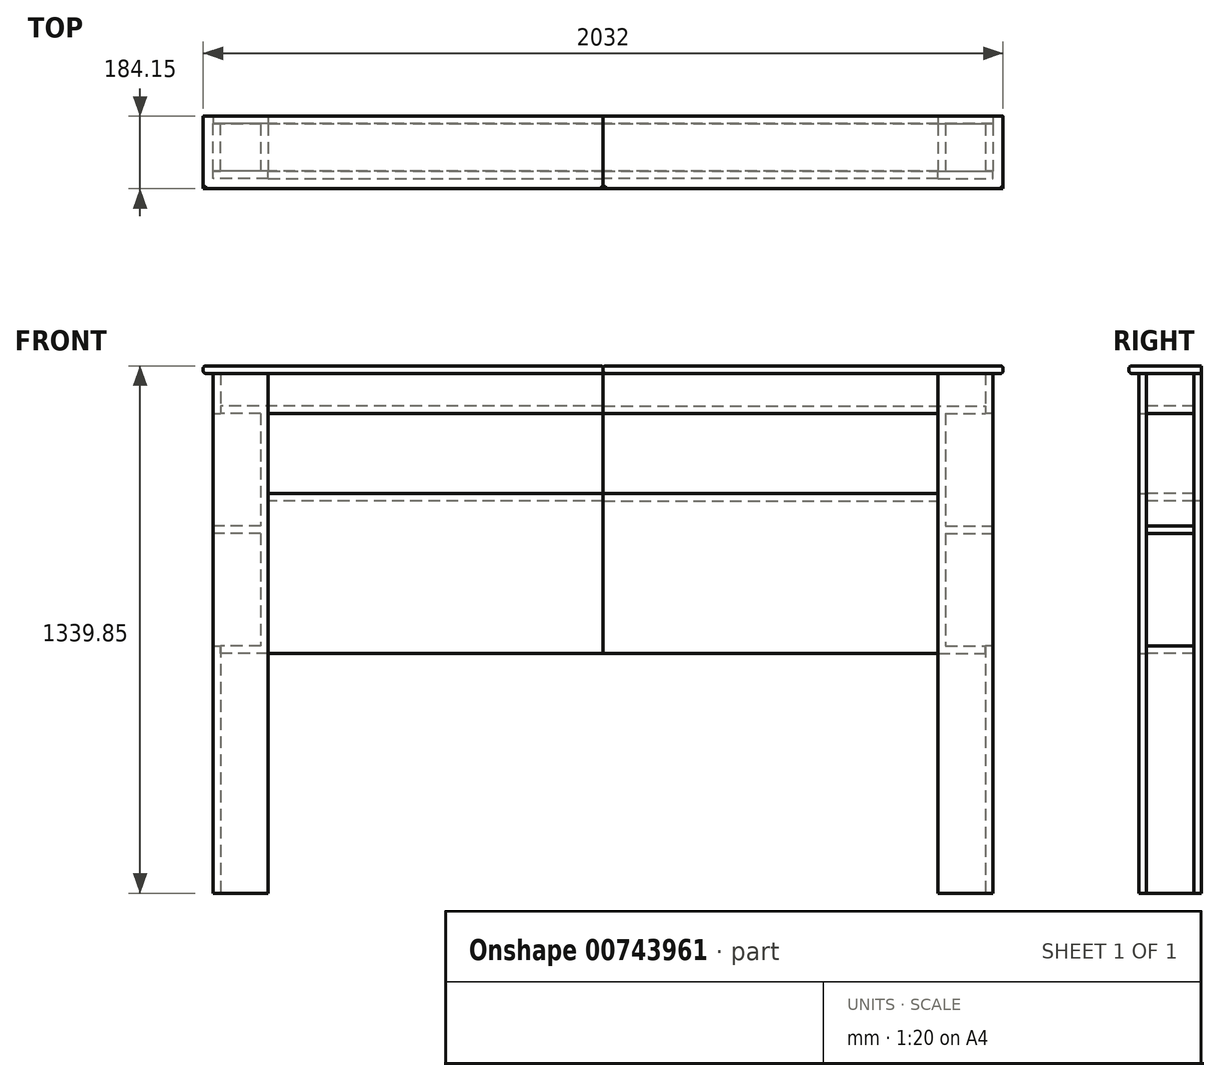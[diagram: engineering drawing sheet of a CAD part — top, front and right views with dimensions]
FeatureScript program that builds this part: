
annotation { "Feature Type Name" : "Feature", "Feature Type Description" : "" }
export const myFeature = defineFeature(function(context is Context, id is Id, definition is map)
    precondition{}
    {
        {
            var Q0;
            Q0=qCreatedBy(makeId("Front.planeOp"),FACE);
            var sketch = newSketch(context, id + "F0", { "sketchPlane" : qUnion([Q0])});
            skLineSegment(sketch, "E0.bottom", {"start": v(850.9, 0) * mm, "end": v(990.6, 0) * mm});
            skLineSegment(sketch, "E0.top", {"start": v(850.9, 1320.8) * mm, "end": v(990.6, 1320.8) * mm});
            skLineSegment(sketch, "E0.left", {"start": v(850.9, 0) * mm, "end": v(850.9, 1320.8) * mm});
            skLineSegment(sketch, "E0.right", {"start": v(990.6, 0) * mm, "end": v(990.6, 1320.8) * mm});
            skSolve(sketch);
        }
        {
            var Q0;
            Q0 = qSketchRegion(id + "F0", true);
            extrude(context, id + "F1", {"entities" : qUnion([Q0]), "depth" : 19.05 * mm, "offsetDistance" : 25.4 * mm});
        }
        {
            var Q0;
            Q0=qCreatedBy(makeId("Front.planeOp"),FACE);
            var sketch = newSketch(context, id + "F2", { "sketchPlane" : qUnion([Q0])});
            skLineSegment(sketch, "E1.bottom", {"start": v(850.9, 609.6) * mm, "end": v(0, 609.6) * mm});
            skLineSegment(sketch, "E1.top", {"start": v(850.9, 1016) * mm, "end": v(0, 1016) * mm});
            skLineSegment(sketch, "E1.left", {"start": v(850.9, 609.6) * mm, "end": v(850.9, 1016) * mm});
            skLineSegment(sketch, "E1.right", {"start": v(0, 609.6) * mm, "end": v(0, 1016) * mm});
            skSolve(sketch);
        }
        {
            var Q0;
            Q0 = qSketchRegion(id + "F2", true);
            extrude(context, id + "F3", {"entities" : qUnion([Q0]), "depth" : 19.05 * mm, "offsetDistance" : 25.4 * mm});
        }
        {
            var Q0;
            Q0=qCreatedBy(makeId("Front.planeOp"),FACE);
            var sketch = newSketch(context, id + "F4", { "sketchPlane" : qUnion([Q0])});
            skLineSegment(sketch, "E2.bottom", {"start": v(0, 1016) * mm, "end": v(850.9, 1016) * mm});
            skLineSegment(sketch, "E2.top", {"start": v(0, 996.95) * mm, "end": v(850.9, 996.95) * mm});
            skLineSegment(sketch, "E2.left", {"start": v(0, 1016) * mm, "end": v(0, 996.95) * mm});
            skLineSegment(sketch, "E3.left", {"start": v(850.9, 1219.2) * mm, "end": v(850.9, 1016) * mm});
            skLineSegment(sketch, "E3.right", {"start": v(869.95, 1219.2) * mm, "end": v(869.95, 933.57) * mm});
            skLineSegment(sketch, "E4.bottom", {"start": v(850.9, 1219.2) * mm, "end": v(0, 1219.2) * mm});
            skLineSegment(sketch, "E4.top", {"start": v(869.95, 1238.25) * mm, "end": v(0, 1238.25) * mm});
            skLineSegment(sketch, "E4.right", {"start": v(0, 1219.2) * mm, "end": v(0, 1238.25) * mm});
            skLineSegment(sketch, "E5.bottom", {"start": v(869.95, 1238.25) * mm, "end": v(971.55, 1238.25) * mm});
            skLineSegment(sketch, "E5.top", {"start": v(869.95, 1219.2) * mm, "end": v(971.55, 1219.2) * mm});
            skLineSegment(sketch, "E6", {"start": v(971.55, 1238.25) * mm, "end": v(971.55, 1219.2) * mm});
            skLineSegment(sketch, "E7", {"start": v(850.9, 609.6) * mm, "end": v(869.95, 609.6) * mm});
            skLineSegment(sketch, "E8", {"start": v(850.9, 609.6) * mm, "end": v(850.9, 996.95) * mm});
            skLineSegment(sketch, "E9.bottom", {"start": v(869.95, 609.6) * mm, "end": v(971.55, 609.6) * mm});
            skLineSegment(sketch, "E9.top", {"start": v(869.95, 628.9) * mm, "end": v(971.55, 628.9) * mm});
            skLineSegment(sketch, "E10.bottom", {"start": v(869.95, 914.52) * mm, "end": v(990.6, 914.52) * mm});
            skLineSegment(sketch, "E10.top", {"start": v(869.95, 933.57) * mm, "end": v(990.6, 933.57) * mm});
            skLineSegment(sketch, "E10.right", {"start": v(990.6, 914.52) * mm, "end": v(990.6, 933.57) * mm});
            skLineSegment(sketch, "E11.trimOffspring", {"start": v(869.95, 914.52) * mm, "end": v(869.95, 628.9) * mm});
            skLineSegment(sketch, "E12", {"start": v(971.55, 609.6) * mm, "end": v(971.55, 628.9) * mm});
            skSolve(sketch);
        }
        {
            var Q0;
            Q0 = qSketchRegion(id + "F4", true);
            extrude(context, id + "F5", {"entities" : qUnion([Q0]), "oppositeDirection" : true, "depth" : 120.65 * mm, "offsetDistance" : 25.4 * mm});
        }
        {
            var Q0;
            Q0=makeQuery(id+"F5.opExtrude","CAP_FACE",FACE,{"disambiguationData":[OSD([sQuery(id+"F4.wireOp",EDGE,"E2.bottom"),sQuery(id+"F4.wireOp",EDGE,"E2.top"),sQuery(id+"F4.wireOp",EDGE,"E2.left"),sQuery(id+"F4.wireOp",EDGE,"E3.left"),sQuery(id+"F4.wireOp",EDGE,"E3.right"),sQuery(id+"F4.wireOp",EDGE,"E4.bottom"),sQuery(id+"F4.wireOp",EDGE,"E4.top"),sQuery(id+"F4.wireOp",EDGE,"E4.right")])],"isStart":true});
            var sketch = newSketch(context, id + "F6", { "sketchPlane" : qUnion([Q0])});
            skLineSegment(sketch, "E13.bottom", {"start": v(850.9, 1219.2) * mm, "end": v(0, 1219.2) * mm});
            skLineSegment(sketch, "E13.top", {"start": v(850.9, 1320.8) * mm, "end": v(0, 1320.8) * mm});
            skLineSegment(sketch, "E13.left", {"start": v(850.9, 1219.2) * mm, "end": v(850.9, 1320.8) * mm});
            skLineSegment(sketch, "E13.right", {"start": v(0, 1219.2) * mm, "end": v(0, 1320.8) * mm});
            skSolve(sketch);
        }
        {
            var Q0;
            Q0 = qSketchRegion(id + "F6", true);
            extrude(context, id + "F7", {"entities" : qUnion([Q0]), "depth" : 19.05 * mm, "offsetDistance" : 25.4 * mm});
        }
        {
            var Q0;
            Q0=makeQuery(id+"F5.opExtrude","CAP_FACE",FACE,{"disambiguationData":[OSD([sQuery(id+"F4.wireOp",EDGE,"E2.bottom"),sQuery(id+"F4.wireOp",EDGE,"E2.top"),sQuery(id+"F4.wireOp",EDGE,"E2.left"),sQuery(id+"F4.wireOp",EDGE,"E3.left"),sQuery(id+"F4.wireOp",EDGE,"E3.right"),sQuery(id+"F4.wireOp",EDGE,"E4.bottom"),sQuery(id+"F4.wireOp",EDGE,"E4.top"),sQuery(id+"F4.wireOp",EDGE,"E4.right")])],"isStart":false});
            var sketch = newSketch(context, id + "F8", { "sketchPlane" : qUnion([Q0])});
            skLineSegment(sketch, "E14.bottom", {"start": v(0, 996.95) * mm, "end": v(-850.9, 996.95) * mm});
            skLineSegment(sketch, "E14.top", {"start": v(0, 1320.8) * mm, "end": v(-850.9, 1320.8) * mm});
            skLineSegment(sketch, "E14.left", {"start": v(0, 996.95) * mm, "end": v(0, 1320.8) * mm});
            skLineSegment(sketch, "E14.right", {"start": v(-850.9, 996.95) * mm, "end": v(-850.9, 1320.8) * mm});
            skSolve(sketch);
        }
        {
            var Q0;
            Q0 = qSketchRegion(id + "F8", true);
            extrude(context, id + "F9", {"entities" : qUnion([Q0]), "depth" : 19.05 * mm, "offsetDistance" : 25.4 * mm});
        }
        {
            var Q0;
            Q0=makeQuery(id+"F5.opExtrude","SWEPT_FACE",FACE,{"disambiguationData":[OSD([sQuery(id+"F4.wireOp",EDGE,"E6")])]});
            var sketch = newSketch(context, id + "F10", { "sketchPlane" : qUnion([Q0])});
            skLineSegment(sketch, "E15.bottom", {"start": v(0, 1219.2) * mm, "end": v(120.65, 1219.2) * mm});
            skLineSegment(sketch, "E15.top", {"start": v(0, 1320.8) * mm, "end": v(120.65, 1320.8) * mm});
            skLineSegment(sketch, "E15.left", {"start": v(0, 1219.2) * mm, "end": v(0, 1320.8) * mm});
            skLineSegment(sketch, "E15.right", {"start": v(120.65, 1219.2) * mm, "end": v(120.65, 1320.8) * mm});
            skLineSegment(sketch, "E16.bottom", {"start": v(0, 628.9) * mm, "end": v(120.65, 628.9) * mm});
            skLineSegment(sketch, "E16.top", {"start": v(0, 0) * mm, "end": v(120.65, 0) * mm});
            skLineSegment(sketch, "E16.left", {"start": v(0, 628.9) * mm, "end": v(0, 0) * mm});
            skLineSegment(sketch, "E16.right", {"start": v(120.65, 628.9) * mm, "end": v(120.65, 0) * mm});
            skSolve(sketch);
        }
        {
            var Q0;
            Q0 = qSketchRegion(id + "F10", true);
            extrude(context, id + "F11", {"entities" : qUnion([Q0]), "depth" : 19.05 * mm, "offsetDistance" : 25.4 * mm});
        }
        {
            var Q0;
            Q0=makeQuery(id+"F5.opExtrude","CAP_FACE",FACE,{"disambiguationData":[OSD([sQuery(id+"F4.wireOp",EDGE,"E2.bottom"),sQuery(id+"F4.wireOp",EDGE,"E2.top"),sQuery(id+"F4.wireOp",EDGE,"E2.left"),sQuery(id+"F4.wireOp",EDGE,"E3.left"),sQuery(id+"F4.wireOp",EDGE,"E3.right"),sQuery(id+"F4.wireOp",EDGE,"E4.bottom"),sQuery(id+"F4.wireOp",EDGE,"E4.top"),sQuery(id+"F4.wireOp",EDGE,"E4.right"),sQuery(id+"F4.wireOp",EDGE,"E5.bottom"),sQuery(id+"F4.wireOp",EDGE,"E5.top"),sQuery(id+"F4.wireOp",EDGE,"E6"),sQuery(id+"F4.wireOp",EDGE,"E7"),sQuery(id+"F4.wireOp",EDGE,"E8"),sQuery(id+"F4.wireOp",EDGE,"E9.bottom"),sQuery(id+"F4.wireOp",EDGE,"E9.top"),sQuery(id+"F4.wireOp",EDGE,"E10.bottom"),sQuery(id+"F4.wireOp",EDGE,"E10.top"),sQuery(id+"F4.wireOp",EDGE,"E10.right"),sQuery(id+"F4.wireOp",EDGE,"E11.trimOffspring"),sQuery(id+"F4.wireOp",EDGE,"E12")])],"isStart":false});
            var sketch = newSketch(context, id + "F12", { "sketchPlane" : qUnion([Q0])});
            skPoint(sketch, "E17.oppositeSnap0", {"position": v(-850.9, 803.27) * mm});
            skLineSegment(sketch, "E17.bottom", {"start": v(-990.6, 1320.8) * mm, "end": v(-850.9, 1320.8) * mm});
            skLineSegment(sketch, "E17.top", {"start": v(-990.6, 0) * mm, "end": v(-850.9, 0) * mm});
            skLineSegment(sketch, "E17.left", {"start": v(-990.6, 1320.8) * mm, "end": v(-990.6, 0) * mm});
            skLineSegment(sketch, "E17.right", {"start": v(-850.9, 1320.8) * mm, "end": v(-850.9, 0) * mm});
            skSolve(sketch);
        }
        {
            var Q0;
            Q0 = qSketchRegion(id + "F12", true);
            extrude(context, id + "F13", {"entities" : qUnion([Q0]), "depth" : 19.05 * mm, "offsetDistance" : 25.4 * mm});
        }
        {
            var Q0;
            Q0=makeQuery(id+"F9.opExtrude","SWEPT_FACE",FACE,{"disambiguationData":[OSD([sQuery(id+"F8.wireOp",EDGE,"E14.top")])]});
            var sketch = newSketch(context, id + "F14", { "sketchPlane" : qUnion([Q0])});
            skLineSegment(sketch, "E18.bottom", {"start": v(1016, 139.7) * mm, "end": v(0, 139.7) * mm});
            skLineSegment(sketch, "E18.top", {"start": v(1016, -44.45) * mm, "end": v(0, -44.45) * mm});
            skLineSegment(sketch, "E18.left", {"start": v(1016, 139.7) * mm, "end": v(1016, -44.45) * mm});
            skLineSegment(sketch, "E18.right", {"start": v(0, 139.7) * mm, "end": v(0, -44.45) * mm});
            skSolve(sketch);
        }
        {
            var Q0;
            Q0 = qSketchRegion(id + "F14", true);
            extrude(context, id + "F15", {"entities" : qUnion([Q0]), "depth" : 19.05 * mm, "offsetDistance" : 25.4 * mm});
        }
        {
            var Q0;
            Q0=makeQuery(id+"F15.opExtrude","CAP_EDGE",EDGE,{"disambiguationData":[OSD([sQuery(id+"F14.wireOp",EDGE,"E18.left")])],"isStart":false});
            var Q1;
            Q1=makeQuery(id+"F15.opExtrude","CAP_EDGE",EDGE,{"disambiguationData":[OSD([sQuery(id+"F14.wireOp",EDGE,"E18.top")])],"isStart":false});
            var Q2;
            Q2=makeQuery(id+"F15.opExtrude","CAP_EDGE",EDGE,{"disambiguationData":[OSD([sQuery(id+"F14.wireOp",EDGE,"E18.top")])],"isStart":true});
            var Q3;
            Q3=makeQuery(id+"F15.opExtrude","CAP_EDGE",EDGE,{"disambiguationData":[OSD([sQuery(id+"F14.wireOp",EDGE,"E18.left")])],"isStart":true});
            var Q4;
            Q4=makeQuery(id+"F15.opExtrude","CAP_EDGE",EDGE,{"disambiguationData":[OSD([sQuery(id+"F14.wireOp",EDGE,"E18.right")])],"isStart":false});
            var Q5;
            Q5=makeQuery(id+"F15.opExtrude","CAP_EDGE",EDGE,{"disambiguationData":[OSD([sQuery(id+"F14.wireOp",EDGE,"E18.right")])],"isStart":true});
            fillet(context, id + "F16", {"entities" : qUnion([Q0, Q1, Q2, Q3, Q4, Q5]), "radius" : 6.35 * mm, "tangentPropagation" : true, "allowEdgeOverflow" : false});
        }
        {
            var Q0;
            Q0=makeQuery(id+"F15.opExtrude","SWEPT_BODY",BODY,{"disambiguationData":[OSD([sQuery(id+"F14.wireOp",EDGE,"E18.bottom"),sQuery(id+"F14.wireOp",EDGE,"E18.top"),sQuery(id+"F14.wireOp",EDGE,"E18.left"),sQuery(id+"F14.wireOp",EDGE,"E18.right")])]});
            var Q1;
            Q1=makeQuery(id+"F1.opExtrude","SWEPT_BODY",BODY,{"disambiguationData":[OSD([sQuery(id+"F0.wireOp",EDGE,"E0.bottom"),sQuery(id+"F0.wireOp",EDGE,"E0.top"),sQuery(id+"F0.wireOp",EDGE,"E0.left"),sQuery(id+"F0.wireOp",EDGE,"E0.right")])]});
            var Q2;
            Q2=makeQuery(id+"F3.opExtrude","SWEPT_BODY",BODY,{"disambiguationData":[OSD([sQuery(id+"F2.wireOp",EDGE,"E1.bottom"),sQuery(id+"F2.wireOp",EDGE,"E1.top"),sQuery(id+"F2.wireOp",EDGE,"E1.left"),sQuery(id+"F2.wireOp",EDGE,"E1.right")])]});
            var Q3;
            Q3=makeQuery(id+"F5.opExtrude","SWEPT_BODY",BODY,{"disambiguationData":[OSD([sQuery(id+"F4.wireOp",EDGE,"E2.bottom"),sQuery(id+"F4.wireOp",EDGE,"E2.top"),sQuery(id+"F4.wireOp",EDGE,"E2.left"),sQuery(id+"F4.wireOp",EDGE,"E3.left"),sQuery(id+"F4.wireOp",EDGE,"E3.right"),sQuery(id+"F4.wireOp",EDGE,"E4.bottom"),sQuery(id+"F4.wireOp",EDGE,"E4.top"),sQuery(id+"F4.wireOp",EDGE,"E4.right"),sQuery(id+"F4.wireOp",EDGE,"E5.bottom"),sQuery(id+"F4.wireOp",EDGE,"E5.top"),sQuery(id+"F4.wireOp",EDGE,"E6"),sQuery(id+"F4.wireOp",EDGE,"E7"),sQuery(id+"F4.wireOp",EDGE,"E8"),sQuery(id+"F4.wireOp",EDGE,"E9.bottom"),sQuery(id+"F4.wireOp",EDGE,"E9.top"),sQuery(id+"F4.wireOp",EDGE,"E10.bottom"),sQuery(id+"F4.wireOp",EDGE,"E10.top"),sQuery(id+"F4.wireOp",EDGE,"E10.right"),sQuery(id+"F4.wireOp",EDGE,"E11.trimOffspring"),sQuery(id+"F4.wireOp",EDGE,"E12")])]});
            var Q4;
            Q4=makeQuery(id+"F7.opExtrude","SWEPT_BODY",BODY,{"disambiguationData":[OSD([sQuery(id+"F6.wireOp",EDGE,"E13.bottom"),sQuery(id+"F6.wireOp",EDGE,"E13.top"),sQuery(id+"F6.wireOp",EDGE,"E13.left"),sQuery(id+"F6.wireOp",EDGE,"E13.right")])]});
            var Q5;
            Q5=makeQuery(id+"F9.opExtrude","SWEPT_BODY",BODY,{"disambiguationData":[OSD([sQuery(id+"F8.wireOp",EDGE,"E14.bottom"),sQuery(id+"F8.wireOp",EDGE,"E14.top"),sQuery(id+"F8.wireOp",EDGE,"E14.left"),sQuery(id+"F8.wireOp",EDGE,"E14.right")])]});
            var Q6;
            Q6=makeQuery(id+"F11.opExtrude","SWEPT_BODY",BODY,{"disambiguationData":[OSD([sQuery(id+"F10.wireOp",EDGE,"E16.bottom"),sQuery(id+"F10.wireOp",EDGE,"E16.top"),sQuery(id+"F10.wireOp",EDGE,"E16.left"),sQuery(id+"F10.wireOp",EDGE,"E16.right")])]});
            var Q7;
            Q7=makeQuery(id+"F13.opExtrude","SWEPT_BODY",BODY,{"disambiguationData":[OSD([sQuery(id+"F12.wireOp",EDGE,"E17.bottom"),sQuery(id+"F12.wireOp",EDGE,"E17.top"),sQuery(id+"F12.wireOp",EDGE,"E17.left"),sQuery(id+"F12.wireOp",EDGE,"E17.right")])]});
            var Q8;
            Q8=makeQuery(id+"F11.opExtrude","SWEPT_BODY",BODY,{"disambiguationData":[OSD([sQuery(id+"F10.wireOp",EDGE,"E15.bottom"),sQuery(id+"F10.wireOp",EDGE,"E15.top"),sQuery(id+"F10.wireOp",EDGE,"E15.left"),sQuery(id+"F10.wireOp",EDGE,"E15.right")])]});
            var Q9;
            Q9=qCreatedBy(makeId("Right.planeOp"),FACE);
            mirror(context, id + "F17", {"entities" : qUnion([Q0, Q1, Q2, Q3, Q4, Q5, Q6, Q7, Q8]), "mirrorPlane" : qUnion([Q9])});
        }
    });
